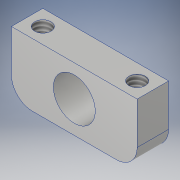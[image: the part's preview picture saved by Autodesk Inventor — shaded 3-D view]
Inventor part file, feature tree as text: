
AUTODESK INVENTOR PART (.ipt)
format: ipt  version: 2017 (Build 210142000, 142)  size: 121,344 bytes
history: native  units: in
note: dims shown in document units (in); Inventor stores cm internally (conversion verified against a paired STEP export)
features: other x3, sketch x2
ambient origin geometry x8: Origin, YZ Plane, XZ Plane, XY Plane, X Axis, Y Axis, Z Axis, Center Point
bodies: Solid1 (feature_tree)
feature tree (5):
  other  "WheelSuspensionHub.ipt"
  other  "Solid1::WheelSuspensionHub.ipt"
  other  "TaggingFeature1"
  sketch  "Sketch1"  dims[d0=0.3937in]
  sketch  "Sketch2"
